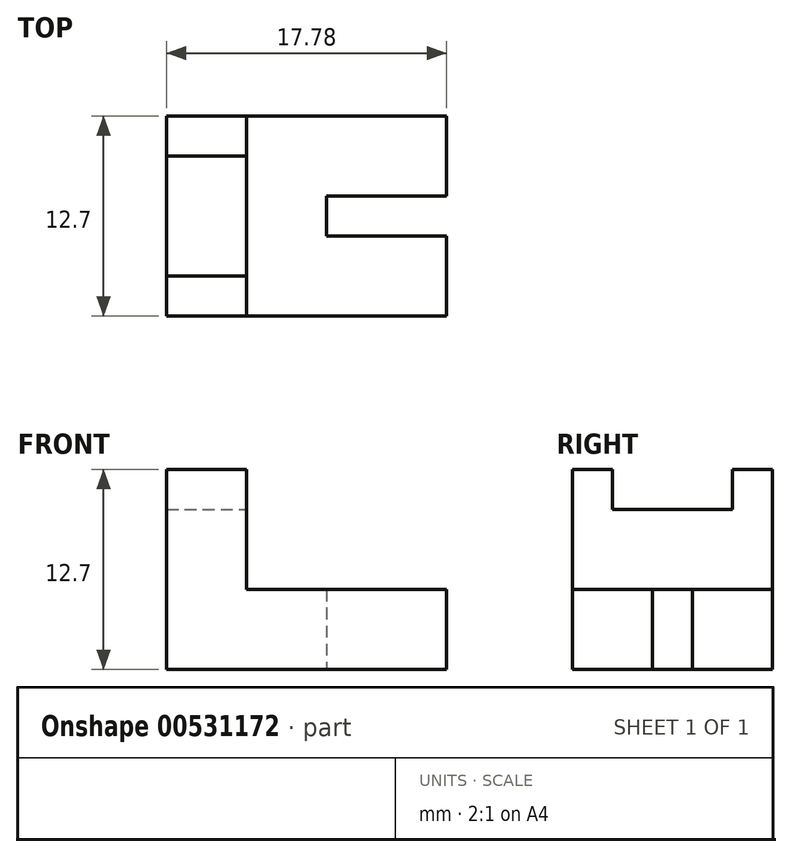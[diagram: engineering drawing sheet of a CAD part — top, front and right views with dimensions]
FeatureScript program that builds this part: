
annotation { "Feature Type Name" : "Feature", "Feature Type Description" : "" }
export const myFeature = defineFeature(function(context is Context, id is Id, definition is map)
    precondition{}
    {
        {
            var Q0;
            Q0=qCreatedBy(makeId("Front.planeOp"),FACE);
            var sketch = newSketch(context, id + "F0", { "sketchPlane" : qUnion([Q0])});
            skLineSegment(sketch, "E0", {"start": v(0, 0) * mm, "end": v(0, 12.7) * mm});
            skLineSegment(sketch, "E1", {"start": v(0, 12.7) * mm, "end": v(5.08, 12.7) * mm});
            skLineSegment(sketch, "E2", {"start": v(5.08, 12.7) * mm, "end": v(5.08, 5.08) * mm});
            skLineSegment(sketch, "E3", {"start": v(5.08, 5.08) * mm, "end": v(17.78, 5.08) * mm});
            skLineSegment(sketch, "E4", {"start": v(17.78, 5.08) * mm, "end": v(17.78, 0) * mm});
            skLineSegment(sketch, "E5", {"start": v(17.78, 0) * mm, "end": v(0, 0) * mm});
            skSolve(sketch);
        }
        {
            var Q0;
            Q0=makeQuery(id+"F0.imprint","IMPRINT",FACE,{"disambiguationData":[TD([[makeQuery(id+"F0.imprint","IMPRINT",EDGE,{"derivedFrom":sQuery(id+"F0.wireOp",EDGE,"E0")}),-1.0]])]});
            extrude(context, id + "F1", {"entities" : qUnion([Q0]), "depth" : 2.54 * mm, "offsetDistance" : 25.4 * mm});
        }
        {
            var Q0;
            Q0=makeQuery(id+"F1.opExtrude","CAP_FACE",FACE,{"disambiguationData":[OSD([sQuery(id+"F0.wireOp",EDGE,"E0"),sQuery(id+"F0.wireOp",EDGE,"E1"),sQuery(id+"F0.wireOp",EDGE,"E2"),sQuery(id+"F0.wireOp",EDGE,"E3"),sQuery(id+"F0.wireOp",EDGE,"E4"),sQuery(id+"F0.wireOp",EDGE,"E5")])],"isStart":true});
            var sketch = newSketch(context, id + "F2", { "sketchPlane" : qUnion([Q0])});
            skLineSegment(sketch, "E6", {"start": v(0, 0) * mm, "end": v(0, 10.16) * mm});
            skLineSegment(sketch, "E7", {"start": v(0, 10.16) * mm, "end": v(-5.08, 10.16) * mm});
            skLineSegment(sketch, "E8", {"start": v(-5.08, 10.16) * mm, "end": v(-5.08, 5.08) * mm});
            skLineSegment(sketch, "E9", {"start": v(-5.08, 5.08) * mm, "end": v(-17.78, 5.08) * mm});
            skLineSegment(sketch, "E10", {"start": v(-17.78, 5.08) * mm, "end": v(-17.78, 0) * mm});
            skLineSegment(sketch, "E11", {"start": v(-17.78, 0) * mm, "end": v(0, 0) * mm});
            skSolve(sketch);
        }
        {
            var Q0;
            Q0=makeQuery(id+"F2.imprint","IMPRINT",FACE,{"disambiguationData":[TD([[makeQuery(id+"F2.imprint","IMPRINT",EDGE,{"derivedFrom":sQuery(id+"F2.wireOp",EDGE,"E6")}),1.0]])]});
            extrude(context, id + "F3", {"entities" : qUnion([Q0]), "operationType" : NewBodyOperationType.ADD, "depth" : 2.54 * mm, "offsetDistance" : 25.4 * mm});
        }
        {
            var Q0;
            Q0=makeQuery(id+"F3.opExtrude","CAP_FACE",FACE,{"disambiguationData":[OSD([sQuery(id+"F2.wireOp",EDGE,"E6"),sQuery(id+"F2.wireOp",EDGE,"E7"),sQuery(id+"F2.wireOp",EDGE,"E8"),sQuery(id+"F2.wireOp",EDGE,"E9"),sQuery(id+"F2.wireOp",EDGE,"E10"),sQuery(id+"F2.wireOp",EDGE,"E11")])],"isStart":false});
            var sketch = newSketch(context, id + "F4", { "sketchPlane" : qUnion([Q0])});
            skLineSegment(sketch, "E12", {"start": v(0, 10.16) * mm, "end": v(-5.08, 10.16) * mm});
            skLineSegment(sketch, "E13", {"start": v(-5.08, 10.16) * mm, "end": v(-5.08, 5.08) * mm});
            skLineSegment(sketch, "E14", {"start": v(-5.08, 5.08) * mm, "end": v(-10.16, 5.08) * mm});
            skLineSegment(sketch, "E15", {"start": v(-10.16, 5.08) * mm, "end": v(-10.16, 0) * mm});
            skLineSegment(sketch, "E16", {"start": v(-10.16, 0) * mm, "end": v(0, 0) * mm});
            skLineSegment(sketch, "E17", {"start": v(0, 0) * mm, "end": v(0, 10.16) * mm});
            skSolve(sketch);
        }
        {
            var Q0;
            Q0=makeQuery(id+"F4.imprint","IMPRINT",FACE,{"disambiguationData":[TD([[makeQuery(id+"F4.imprint","IMPRINT",EDGE,{"derivedFrom":sQuery(id+"F4.wireOp",EDGE,"E12")}),1.0]])]});
            extrude(context, id + "F5", {"entities" : qUnion([Q0]), "operationType" : NewBodyOperationType.ADD, "depth" : 2.54 * mm, "offsetDistance" : 25.4 * mm});
        }
        {
            var Q0;
            Q0=makeQuery(id+"F5.opExtrude","CAP_FACE",FACE,{"disambiguationData":[OSD([sQuery(id+"F4.wireOp",EDGE,"E12"),sQuery(id+"F4.wireOp",EDGE,"E13"),sQuery(id+"F4.wireOp",EDGE,"E14"),sQuery(id+"F4.wireOp",EDGE,"E15"),sQuery(id+"F4.wireOp",EDGE,"E16"),sQuery(id+"F4.wireOp",EDGE,"E17")])],"isStart":false});
            var sketch = newSketch(context, id + "F6", { "sketchPlane" : qUnion([Q0])});
            skLineSegment(sketch, "E18", {"start": v(0, 0) * mm, "end": v(-17.78, 0) * mm});
            skLineSegment(sketch, "E19", {"start": v(-17.78, 0) * mm, "end": v(-17.78, 5.08) * mm});
            skLineSegment(sketch, "E20", {"start": v(-17.78, 5.08) * mm, "end": v(-5.08, 5.08) * mm});
            skLineSegment(sketch, "E21", {"start": v(-5.08, 5.08) * mm, "end": v(-5.08, 10.16) * mm});
            skLineSegment(sketch, "E22", {"start": v(-5.08, 10.16) * mm, "end": v(0, 10.16) * mm});
            skLineSegment(sketch, "E23", {"start": v(0, 10.16) * mm, "end": v(0, 0) * mm});
            skSolve(sketch);
        }
        {
            var Q0;
            Q0 = qSketchRegion(id + "F6", true);
            extrude(context, id + "F7", {"entities" : qUnion([Q0]), "operationType" : NewBodyOperationType.ADD, "depth" : 2.54 * mm, "offsetDistance" : 25.4 * mm});
        }
        {
            var Q0;
            Q0=makeQuery(id+"F7.opExtrude","CAP_FACE",FACE,{"disambiguationData":[OSD([sQuery(id+"F6.wireOp",EDGE,"E18"),sQuery(id+"F6.wireOp",EDGE,"E19"),sQuery(id+"F6.wireOp",EDGE,"E20"),sQuery(id+"F6.wireOp",EDGE,"E21"),sQuery(id+"F6.wireOp",EDGE,"E22"),sQuery(id+"F6.wireOp",EDGE,"E23")])],"isStart":false});
            var sketch = newSketch(context, id + "F8", { "sketchPlane" : qUnion([Q0])});
            skLineSegment(sketch, "E24", {"start": v(0, 0) * mm, "end": v(0, 12.7) * mm});
            skPoint(sketch, "E24.endSnap0", {"position": v(0, 5.08) * mm});
            skLineSegment(sketch, "E25", {"start": v(0, 12.7) * mm, "end": v(-5.08, 12.7) * mm});
            skLineSegment(sketch, "E26", {"start": v(-5.08, 12.7) * mm, "end": v(-5.08, 5.08) * mm});
            skLineSegment(sketch, "E27", {"start": v(-5.08, 5.08) * mm, "end": v(-17.78, 5.08) * mm});
            skLineSegment(sketch, "E28", {"start": v(-17.78, 5.08) * mm, "end": v(-17.78, 0) * mm});
            skLineSegment(sketch, "E29", {"start": v(-17.78, 0) * mm, "end": v(0, 0) * mm});
            skSolve(sketch);
        }
        {
            var Q0;
            Q0 = qSketchRegion(id + "F8", true);
            extrude(context, id + "F9", {"entities" : qUnion([Q0]), "operationType" : NewBodyOperationType.ADD, "depth" : 2.54 * mm, "offsetDistance" : 25.4 * mm});
        }
    });
